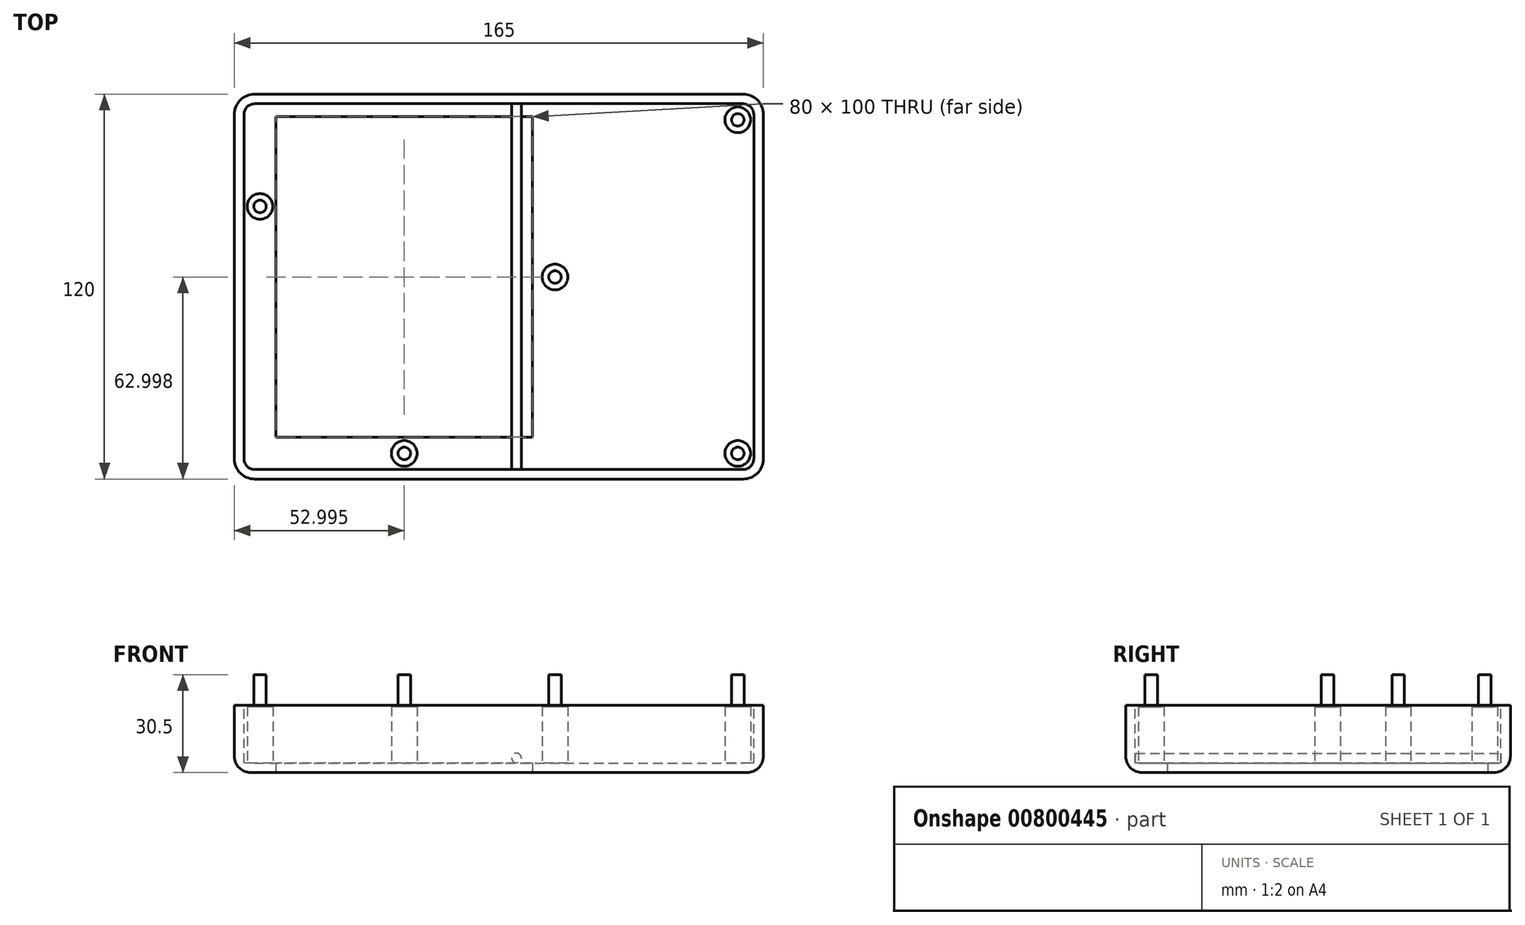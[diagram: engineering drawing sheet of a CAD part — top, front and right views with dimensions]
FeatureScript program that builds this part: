
annotation { "Feature Type Name" : "Feature", "Feature Type Description" : "" }
export const myFeature = defineFeature(function(context is Context, id is Id, definition is map)
    precondition{}
    {
        {
            var Q0;
            Q0=qCreatedBy(makeId("Top.planeOp"),FACE);
            var sketch = newSketch(context, id + "F0", { "sketchPlane" : qUnion([Q0])});
            skLineSegment(sketch, "E0.bottom", {"start": v(-76.98, -45.25) * mm, "end": v(75.32, -45.25) * mm});
            skLineSegment(sketch, "E0.top", {"start": v(-76.98, 74.75) * mm, "end": v(75.32, 74.75) * mm});
            skLineSegment(sketch, "E0.left", {"start": v(-83.33, -38.9) * mm, "end": v(-83.33, 68.4) * mm});
            skLineSegment(sketch, "E0.right", {"start": v(81.67, -38.9) * mm, "end": v(81.67, 68.4) * mm});
            skPoint(sketch, "E1.visualSharp", {"position": v(-83.33, 74.75) * mm});
            skArc(sketch, "E1.filletArc", {"start": v(-76.98, 74.75) * mm, "mid": v(-81.47, 72.89) * mm, "end": v(-83.33, 68.4) * mm});
            skPoint(sketch, "E2.visualSharp", {"position": v(81.67, 74.75) * mm});
            skArc(sketch, "E2.filletArc", {"start": v(81.67, 68.4) * mm, "mid": v(79.8, 72.89) * mm, "end": v(75.32, 74.75) * mm});
            skPoint(sketch, "E3.visualSharp", {"position": v(81.67, -45.25) * mm});
            skArc(sketch, "E3.filletArc", {"start": v(75.32, -45.25) * mm, "mid": v(79.8, -43.4) * mm, "end": v(81.67, -38.9) * mm});
            skPoint(sketch, "E4.visualSharp", {"position": v(-83.33, -45.25) * mm});
            skArc(sketch, "E4.filletArc", {"start": v(-83.33, -38.9) * mm, "mid": v(-81.47, -43.4) * mm, "end": v(-76.98, -45.25) * mm});
            skSolve(sketch);
        }
        {
            var Q0;
            Q0=qSketchRegion(id+"F0",true);
            extrude(context, id + "F1", {"entities" : qUnion([Q0]), "depth" : 21 * mm, "offsetDistance" : 25.4 * mm});
        }
        {
            var Q0;
            Q0=makeQuery(id+"F1.opExtrude","CAP_FACE",FACE,{"disambiguationData":[OSD([sQuery(id+"F0.wireOp",EDGE,"E0.bottom"),sQuery(id+"F0.wireOp",EDGE,"E0.top"),sQuery(id+"F0.wireOp",EDGE,"E0.left"),sQuery(id+"F0.wireOp",EDGE,"E0.right")])],"isStart":false});
            shell(context, id + "F2", {"entities" : qUnion([Q0]), "thickness" : 3 * mm});
        }
        {
            var Q0;
            Q0=makeQuery(id+"F1.opExtrude","CAP_EDGE",EDGE,{"disambiguationData":[OSD([sQuery(id+"F0.wireOp",EDGE,"E1.filletArc")])],"isStart":true});
            fillet(context, id + "F3", {"entities" : qUnion([Q0]), "radius" : 5.08 * mm, "tangentPropagation" : true, "allowEdgeOverflow" : false});
        }
        {
            var Q0;
            Q0=makeQuery(id+"F2.opShell","OFFSET_FACE",FACE,{"disambiguationData":[OSD([sQuery(id+"F0.wireOp",EDGE,"E0.bottom"),sQuery(id+"F0.wireOp",EDGE,"E0.top"),sQuery(id+"F0.wireOp",EDGE,"E0.left"),sQuery(id+"F0.wireOp",EDGE,"E0.right"),sQuery(id+"F0.wireOp",EDGE,"E1.filletArc"),sQuery(id+"F0.wireOp",EDGE,"E2.filletArc"),sQuery(id+"F0.wireOp",EDGE,"E3.filletArc"),sQuery(id+"F0.wireOp",EDGE,"E4.filletArc")])]});
            var sketch = newSketch(context, id + "F4", { "sketchPlane" : qUnion([Q0])});
            skCircle(sketch, "E5", {"center": v(73.67, -37.25) * mm, "radius": 4 * mm});
            skCircle(sketch, "E6", {"center": v(73.67, 66.75) * mm, "radius": 4 * mm});
            skCircle(sketch, "E7", {"center": v(16.67, 17.75) * mm, "radius": 4 * mm});
            skCircle(sketch, "E8", {"center": v(-75.33, 39.75) * mm, "radius": 4 * mm});
            skCircle(sketch, "E9", {"center": v(-30.33, -37.25) * mm, "radius": 4 * mm});
            skSolve(sketch);
        }
        {
            var Q0;
            Q0=qSketchRegion(id+"F4",true);
            extrude(context, id + "F5", {"entities" : qUnion([Q0]), "operationType" : NewBodyOperationType.ADD, "depth" : 17.5 * mm, "offsetDistance" : 25 * mm});
        }
        {
            var Q0;
            Q0=makeQuery(id+"F5.opExtrude","CAP_FACE",FACE,{"disambiguationData":[OSD([sQuery(id+"F4.wireOp",EDGE,"E5")])],"isStart":false});
            var sketch = newSketch(context, id + "F6", { "sketchPlane" : qUnion([Q0])});
            skCircle(sketch, "E10", {"center": v(73.67, -37.25) * mm, "radius": 1.95 * mm});
            skCircle(sketch, "E11", {"center": v(16.67, 17.75) * mm, "radius": 1.95 * mm});
            skCircle(sketch, "E12", {"center": v(73.67, 66.75) * mm, "radius": 1.95 * mm});
            skCircle(sketch, "E13", {"center": v(-30.33, -37.25) * mm, "radius": 1.95 * mm});
            skCircle(sketch, "E14", {"center": v(-75.33, 39.75) * mm, "radius": 1.95 * mm});
            skSolve(sketch);
        }
        {
            var Q0;
            Q0=qSketchRegion(id+"F6",true);
            extrude(context, id + "F7", {"entities" : qUnion([Q0]), "operationType" : NewBodyOperationType.ADD, "depth" : 10 * mm, "offsetDistance" : 25 * mm});
        }
        {
            var Q0;
            Q0=makeQuery(id+"F1.opExtrude","CAP_FACE",FACE,{"disambiguationData":[OSD([sQuery(id+"F0.wireOp",EDGE,"E0.bottom"),sQuery(id+"F0.wireOp",EDGE,"E0.top"),sQuery(id+"F0.wireOp",EDGE,"E0.left"),sQuery(id+"F0.wireOp",EDGE,"E0.right"),sQuery(id+"F0.wireOp",EDGE,"E1.filletArc"),sQuery(id+"F0.wireOp",EDGE,"E2.filletArc"),sQuery(id+"F0.wireOp",EDGE,"E3.filletArc"),sQuery(id+"F0.wireOp",EDGE,"E4.filletArc")])],"isStart":true});
            var sketch = newSketch(context, id + "F8", { "sketchPlane" : qUnion([Q0])});
            skLineSegment(sketch, "E15.bottom", {"start": v(-70.33, -67.75) * mm, "end": v(9.67, -67.75) * mm});
            skLineSegment(sketch, "E15.top", {"start": v(-70.33, 32.25) * mm, "end": v(9.67, 32.25) * mm});
            skLineSegment(sketch, "E15.left", {"start": v(-70.33, -67.75) * mm, "end": v(-70.33, 32.25) * mm});
            skLineSegment(sketch, "E15.right", {"start": v(9.67, -67.75) * mm, "end": v(9.67, 32.25) * mm});
            skSolve(sketch);
        }
        {
            var Q0;
            Q0=qSketchRegion(id+"F8",true);
            extrude(context, id + "F9", {"entities" : qUnion([Q0]), "operationType" : NewBodyOperationType.REMOVE, "oppositeDirection" : true, "depth" : 25 * mm, "offsetDistance" : 25 * mm});
        }
        {
            var Q0;
            Q0=makeQuery(id+"F2.opShell","OFFSET_FACE",FACE,{"disambiguationData":[OSD([sQuery(id+"F0.wireOp",EDGE,"E0.top")])]});
            var sketch = newSketch(context, id + "F10", { "sketchPlane" : qUnion([Q0])});
            skCircle(sketch, "E16", {"center": v(4.67, 4.55) * mm, "radius": 1.5 * mm});
            skSolve(sketch);
        }
        {
            var Q0;
            Q0=qSketchRegion(id+"F10",true);
            extrude(context, id + "F11", {"entities" : qUnion([Q0]), "operationType" : NewBodyOperationType.ADD, "depth" : 115 * mm, "offsetDistance" : 25 * mm});
        }
    });
